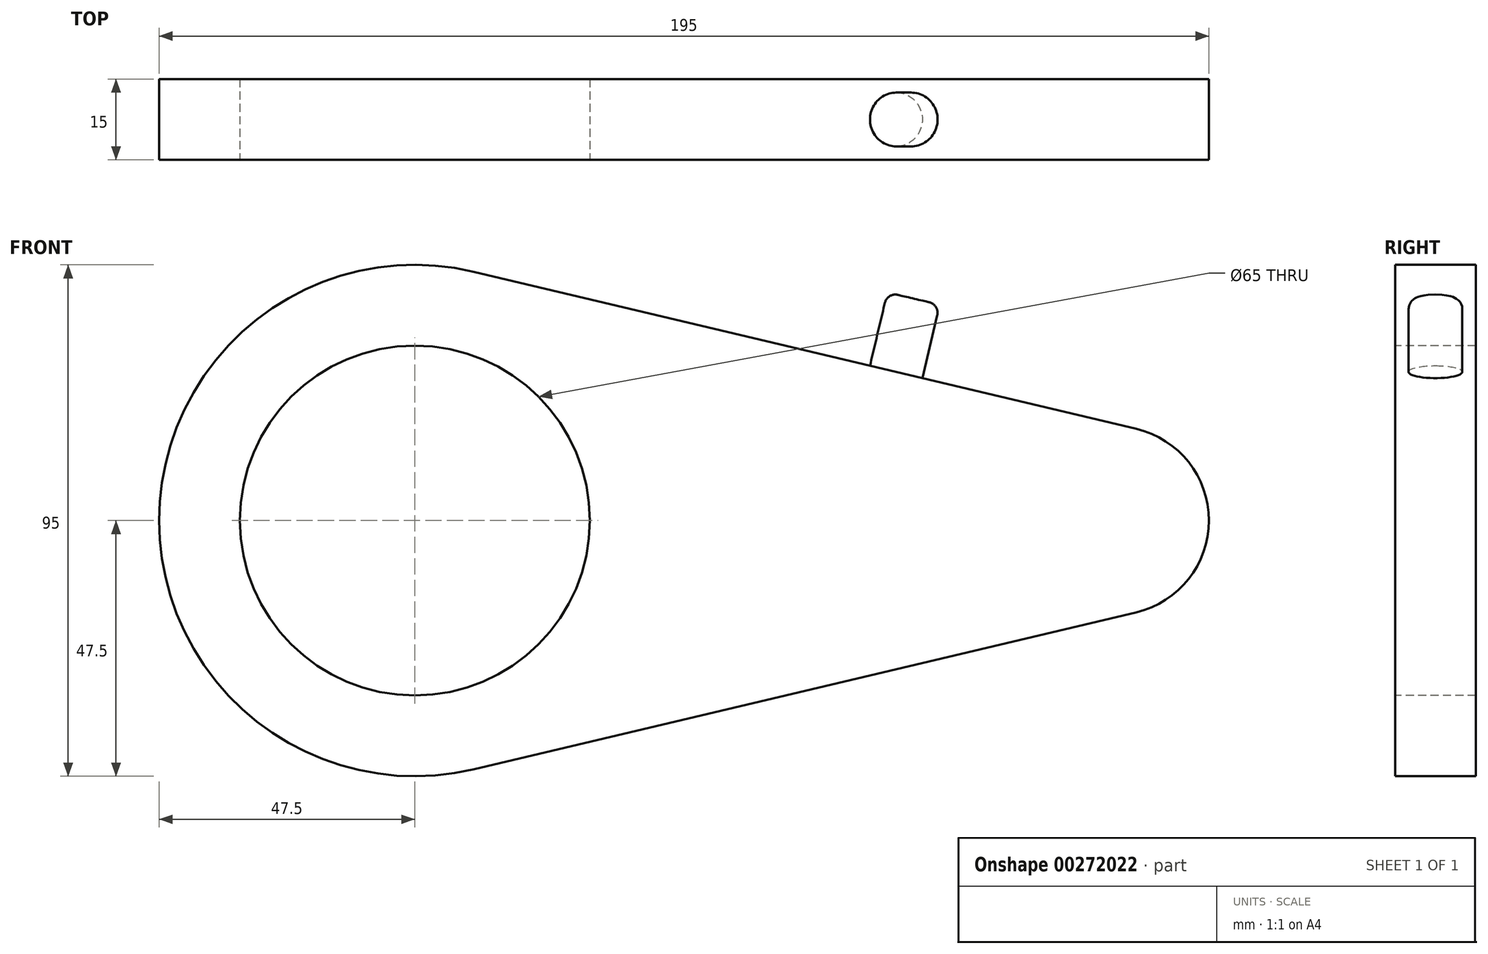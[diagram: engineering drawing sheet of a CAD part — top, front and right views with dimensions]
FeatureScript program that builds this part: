
annotation { "Feature Type Name" : "Feature", "Feature Type Description" : "" }
export const myFeature = defineFeature(function(context is Context, id is Id, definition is map)
    precondition{}
    {
        {
            var Q0;
            Q0=qCreatedBy(makeId("Front.planeOp"),FACE);
            var sketch = newSketch(context, id + "F0", { "sketchPlane" : qUnion([Q0])});
            skCircle(sketch, "E0", {"center": v(0, 0) * mm, "radius": 47.5 * mm});
            skCircle(sketch, "E1", {"center": v(130, 0) * mm, "radius": 17.5 * mm});
            skLineSegment(sketch, "E2", {"start": v(10.96, 46.22) * mm, "end": v(134.04, 17.03) * mm});
            skLineSegment(sketch, "E3", {"start": v(10.96, -46.22) * mm, "end": v(134.04, -17.03) * mm});
            skCircle(sketch, "E4", {"center": v(0, 0) * mm, "radius": 32.5 * mm});
            skSolve(sketch);
        }
        {
            var Q0;
            Q0 = qSketchRegion(id + "F0", true);
            extrude(context, id + "F1", {"entities" : qUnion([Q0]), "oppositeDirection" : true, "depth" : 15 * mm});
        }
        {
            var Q0;
            Q0=makeQuery(id+"F1.opExtrude","SWEPT_FACE",FACE,{"disambiguationData":[OSD([sQuery(id+"F0.wireOp",EDGE,"E2")])]});
            var sketch = newSketch(context, id + "F2", { "sketchPlane" : qUnion([Q0])});
            skCircle(sketch, "E5", {"center": v(80.63, 7.5) * mm, "radius": 5 * mm});
            skPoint(sketch, "E5.centerSnap0", {"position": v(126.5, 7.5) * mm});
            skSolve(sketch);
        }
        {
            var Q0;
            Q0 = qSketchRegion(id + "F2", true);
            extrude(context, id + "F3", {"entities" : qUnion([Q0]), "operationType" : NewBodyOperationType.ADD, "depth" : 14 * mm});
        }
        {
            var Q0;
            Q0=makeQuery(id+"F3.opExtrude","CAP_EDGE",EDGE,{"disambiguationData":[OSD([sQuery(id+"F2.wireOp",EDGE,"E5")])],"isStart":false});
            fillet(context, id + "F4", {"entities" : qUnion([Q0]), "radius" : 2 * mm, "tangentPropagation" : true, "allowEdgeOverflow" : false});
        }
    });
